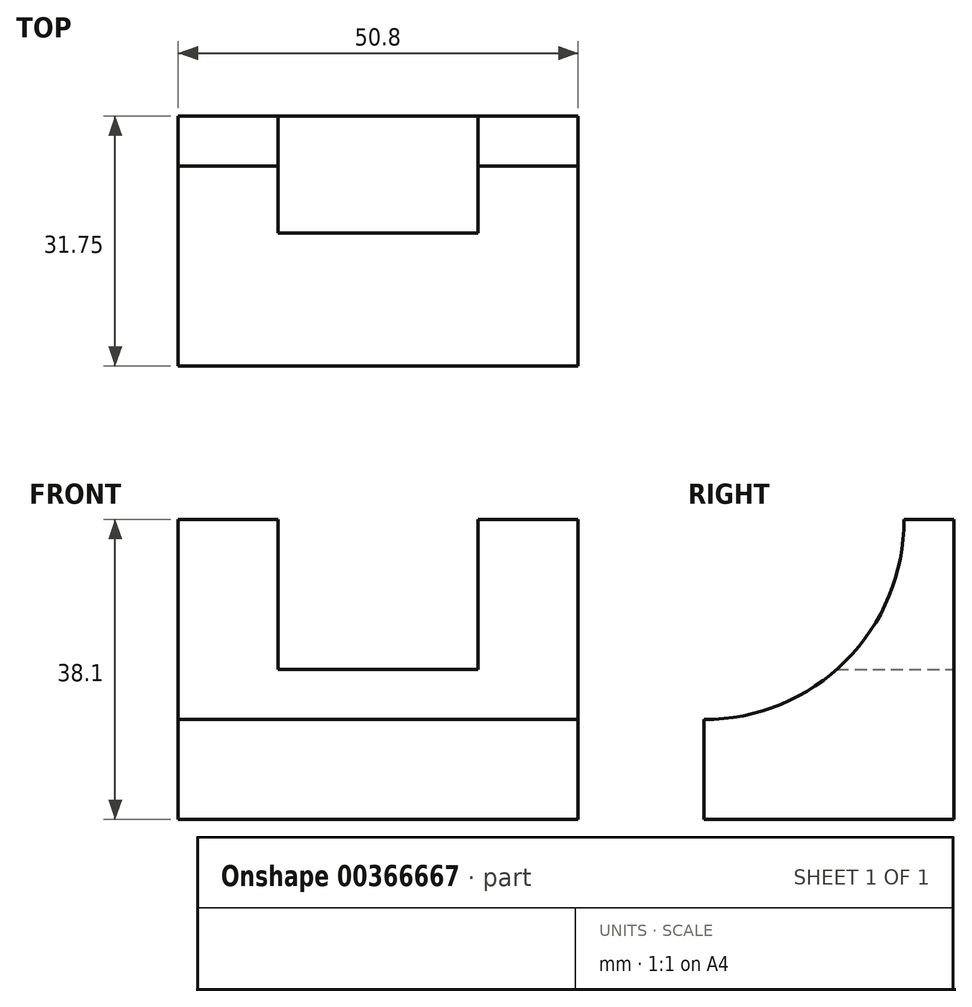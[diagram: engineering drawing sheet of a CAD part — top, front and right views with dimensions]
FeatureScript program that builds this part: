
annotation { "Feature Type Name" : "Feature", "Feature Type Description" : "" }
export const myFeature = defineFeature(function(context is Context, id is Id, definition is map)
    precondition{}
    {
        {
            var Q0;
            Q0=qCreatedBy(makeId("Front.planeOp"),FACE);
            var sketch = newSketch(context, id + "F0", { "sketchPlane" : qUnion([Q0])});
            skLineSegment(sketch, "E0", {"start": v(-59.93, 38.1) * mm, "end": v(-9.13, 38.1) * mm});
            skLineSegment(sketch, "E1", {"start": v(-9.13, 38.1) * mm, "end": v(-9.13, 0) * mm});
            skLineSegment(sketch, "E2", {"start": v(-9.13, 0) * mm, "end": v(-59.93, 0) * mm});
            skLineSegment(sketch, "E3", {"start": v(-59.93, 0) * mm, "end": v(-59.93, 38.1) * mm});
            skSolve(sketch);
        }
        {
            var Q0;
            Q0 = qSketchRegion(id + "F0", true);
            extrude(context, id + "F1", {"entities" : qUnion([Q0]), "depth" : 31.75 * mm});
        }
        {
            var Q0;
            Q0=makeQuery(id+"F1.opExtrude","SWEPT_FACE",FACE,{"disambiguationData":[OSD([sQuery(id+"F0.wireOp",EDGE,"E1")])]});
            var sketch = newSketch(context, id + "F2", { "sketchPlane" : qUnion([Q0])});
            skArc(sketch, "E4", {"start": v(-31.75, 12.7) * mm, "mid": v(-13.76, 20.1) * mm, "end": v(-6.35, 38.1) * mm});
            skSolve(sketch);
        }
        {
            var Q0;
            {var subQ0=sQuery(id+"F2.wireOp",EDGE,"E4");Q0=makeQuery(id+"F2.imprint","IMPRINT",FACE,{"disambiguationData":[TD([[makeQuery(id+"F2.imprint","IMPRINT",EDGE,{"derivedFrom":subQ0}),1.0]])]});}
            extrude(context, id + "F3", {"entities" : qUnion([Q0]), "operationType" : NewBodyOperationType.REMOVE, "oppositeDirection" : true, "depth" : 50.8 * mm});
        }
        {
            var Q0;
            Q0=makeQuery(id+"F1.opExtrude","CAP_FACE",FACE,{"disambiguationData":[OSD([sQuery(id+"F0.wireOp",EDGE,"E0"),sQuery(id+"F0.wireOp",EDGE,"E1"),sQuery(id+"F0.wireOp",EDGE,"E2"),sQuery(id+"F0.wireOp",EDGE,"E3")])],"isStart":true});
            var sketch = newSketch(context, id + "F4", { "sketchPlane" : qUnion([Q0])});
            skLineSegment(sketch, "E5", {"start": v(21.83, 38.1) * mm, "end": v(21.83, 19.05) * mm});
            skLineSegment(sketch, "E6", {"start": v(21.83, 19.05) * mm, "end": v(47.23, 19.05) * mm});
            skLineSegment(sketch, "E7", {"start": v(47.23, 19.05) * mm, "end": v(47.23, 38.1) * mm});
            skSolve(sketch);
        }
        {
            var Q0;
            {var subQ0=sQuery(id+"F4.wireOp",EDGE,"E5");Q0=makeQuery(id+"F4.imprint","IMPRINT",FACE,{"disambiguationData":[TD([[makeQuery(id+"F4.imprint","IMPRINT",EDGE,{"derivedFrom":subQ0}),1.0]])]});}
            extrude(context, id + "F5", {"entities" : qUnion([Q0]), "operationType" : NewBodyOperationType.REMOVE, "oppositeDirection" : true, "depth" : 50.8 * mm});
        }
    });
